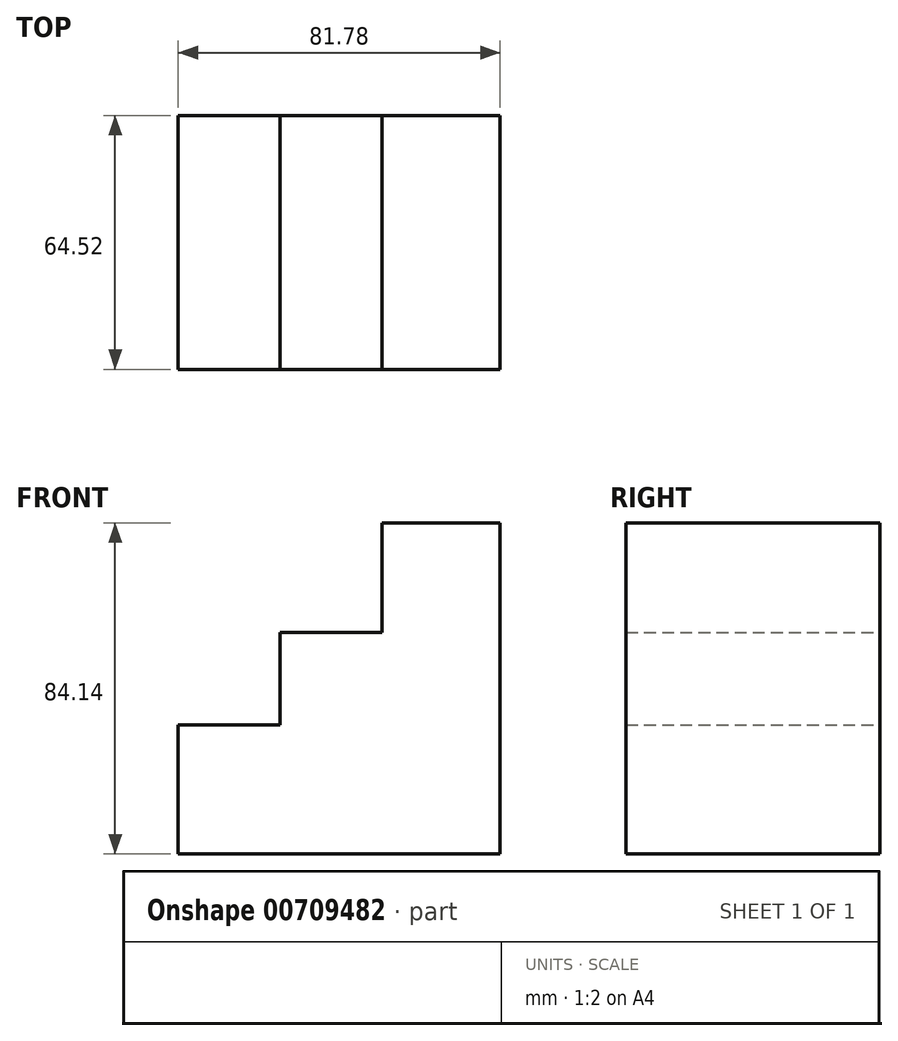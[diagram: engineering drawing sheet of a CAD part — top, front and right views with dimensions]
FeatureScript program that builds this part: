
annotation { "Feature Type Name" : "Feature", "Feature Type Description" : "" }
export const myFeature = defineFeature(function(context is Context, id is Id, definition is map)
    precondition{}
    {
        {
            var Q0;
            Q0=qCreatedBy(makeId("Front.planeOp"),FACE);
            var sketch = newSketch(context, id + "F0", { "sketchPlane" : qUnion([Q0])});
            skLineSegment(sketch, "E0", {"start": v(-50.08, 0) * mm, "end": v(-25.8, 0) * mm});
            skLineSegment(sketch, "E1", {"start": v(-25.8, 0) * mm, "end": v(-25.8, 23.57) * mm});
            skLineSegment(sketch, "E2", {"start": v(-25.8, 23.57) * mm, "end": v(0, 23.57) * mm});
            skLineSegment(sketch, "E3", {"start": v(0, 23.57) * mm, "end": v(0, 51.38) * mm});
            skLineSegment(sketch, "E4", {"start": v(0, 51.38) * mm, "end": v(51.02, 51.38) * mm});
            skLineSegment(sketch, "E5", {"start": v(30.05, 51.38) * mm, "end": v(30.05, -32.76) * mm});
            skLineSegment(sketch, "E6", {"start": v(30.05, -32.76) * mm, "end": v(-51.73, -32.76) * mm});
            skLineSegment(sketch, "E7", {"start": v(-51.73, -32.76) * mm, "end": v(-51.73, 0) * mm});
            skLineSegment(sketch, "E8", {"start": v(-51.73, 0) * mm, "end": v(-50.08, 0) * mm});
            skSolve(sketch);
        }
        {
            var Q0;
            Q0=makeQuery(id+"F0.imprint","IMPRINT",FACE,{"disambiguationData":[TD([[makeQuery(id+"F0.imprint","IMPRINT",EDGE,{"derivedFrom":sQuery(id+"F0.wireOp",EDGE,"E0")}),-1.0]])]});
            extrude(context, id + "F1", {"entities" : qUnion([Q0]), "depth" : 64.52 * mm, "offsetDistance" : 25.4 * mm});
        }
    });
